# Revit family: for update_60157XXX_new
name_source: partatom
category: Plumbing Fixtures
revit_build: Autodesk Revit 2018 (Build: 20170223_1515(x64)
units: mm (PartAtom-declared; Revit-internal decimal feet)

## family parameters
Cut with Voids When Loaded = No
Host = Face
OmniClass Number = 23.45.05.14.14
OmniClass Title = Sinks/Lavatories
Part Type = Normal
Room Calculation Point = No
Round Connector Dimension = Use Diameter
Shared = No

## types (1)
- 450 White
    BIMobject category = Wash Basins
    Default Elevation = 1219 mm
    Description = OpenTide U Above counter basin 550/400 with overflow
    Design country = Germany
    Edition number = 1
    IFC Classification = Sanitary Terminal
    Installation instructions = https://www.hansgrohe.com
    Manufacturer = Hansgrohe
    Manufacturer country = Germany
    Manufacturer name = hansgrohe
    Masterformat 2014 Code = 22 41 16.16
    Masterformat 2014 Description = Residential Sinks
    Material = Hansgrohe - Ceramic - 450 White
    Model = 60157XXX
    OmniClass Code = 23-31 13 00
    OmniClass Description = Sinks
    Product Guid = 8c6cbe0d-5b2a-4324-be17-0b4c69039f90
    Product SKU = 60157XXX
    Product data url = https://bimobject.com
    Product family = OpenTide U
    Product group = Washbasins
    Product name = 60157XXX OpenTide U Above counter basin 550/400 with overflow
    Product url = https://www.hansgrohe.com
    QR code = https://bimobject.com
    URL = https://www.hansgrohe.com
    Uniclass 2015 Code = Pr_40_20_96
    Uniclass 2015 Name = Wash basins, sinks and troughs
    Uniformat II Code = D2010
    Uniformat II Description = Plumbing Fixtures
    Water Outlet = 46  [stored 0.150919 ft]
    Water Outlet Description = Water Outlet 46 mm

note: [stored X ft] marks values corroborated as IEEE doubles in the binary element streams (Revit-internal decimal feet)

## geometry (parser evidence)
native form markers: Sweep x6
no freeform markers — native parametric forms only
